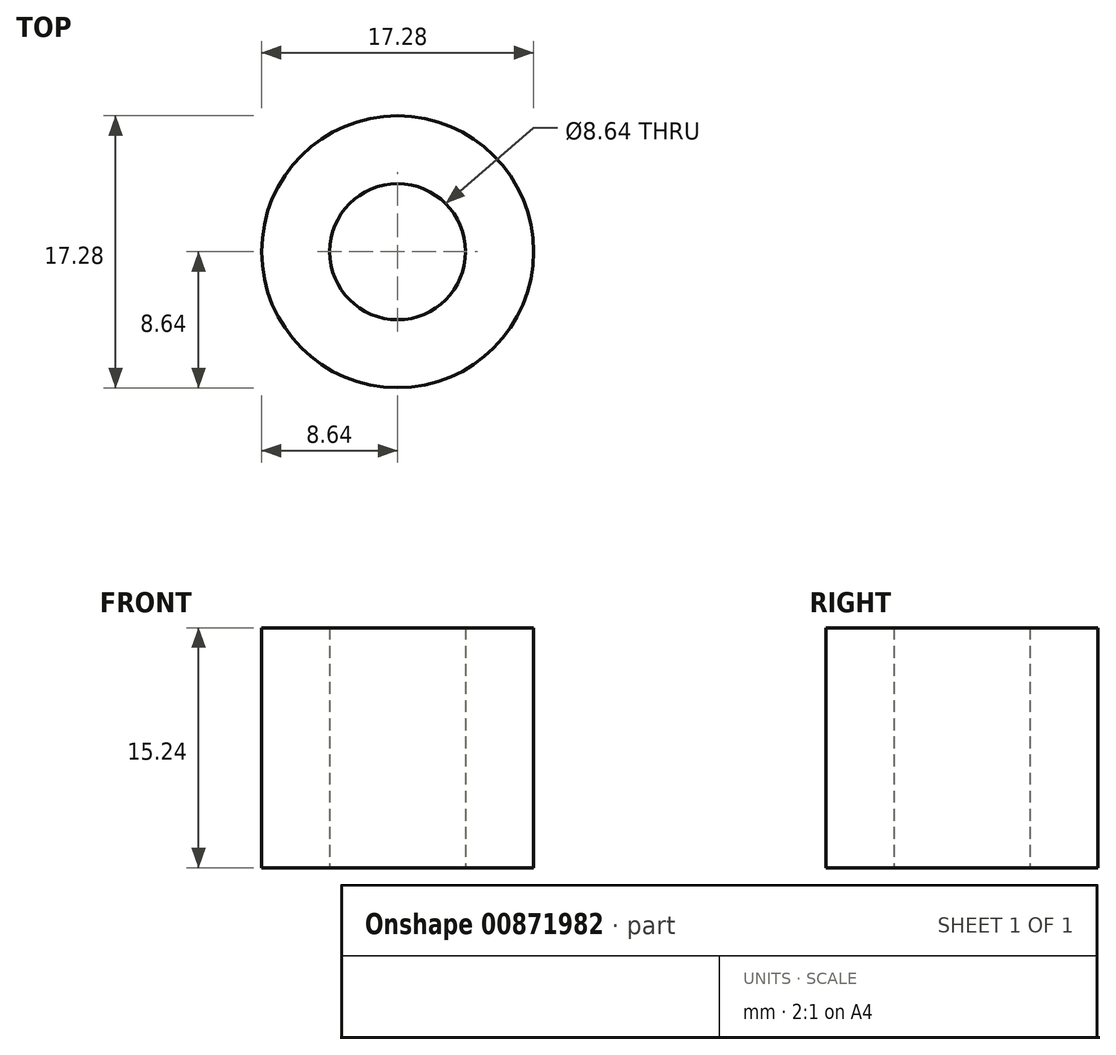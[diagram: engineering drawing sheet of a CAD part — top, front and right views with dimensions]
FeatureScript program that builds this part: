
annotation { "Feature Type Name" : "Feature", "Feature Type Description" : "" }
export const myFeature = defineFeature(function(context is Context, id is Id, definition is map)
    precondition{}
    {
        {
            var Q0;
            Q0=qCreatedBy(makeId("Front.planeOp"),FACE);
            var sketch = newSketch(context, id + "F0", { "sketchPlane" : qUnion([Q0])});
            skLineSegment(sketch, "E0", {"start": v(0, 0) * mm, "end": v(0, 15.24) * mm, "construction": true});
            skLineSegment(sketch, "E1", {"start": v(4.32, 0) * mm, "end": v(8.64, 0) * mm});
            skLineSegment(sketch, "E2", {"start": v(8.64, 0) * mm, "end": v(8.64, 15.24) * mm});
            skLineSegment(sketch, "E3", {"start": v(8.64, 15.24) * mm, "end": v(4.32, 15.24) * mm});
            skLineSegment(sketch, "E4", {"start": v(4.32, 15.24) * mm, "end": v(4.32, 0) * mm});
            skSolve(sketch);
        }
        {
            var Q0;
            Q0=qSketchRegion(id+"F0",true);
            var Q1;
            Q1=sQuery(id+"F0.wireOp",EDGE,"E0");
            revolve(context, id + "F1", {"surfaceOperationType" : NewSurfaceOperationType.NEW, "entities" : qUnion([Q0]), "axis" : qUnion([Q1]), "revolveType" : RevolveType.FULL});
        }
    });
